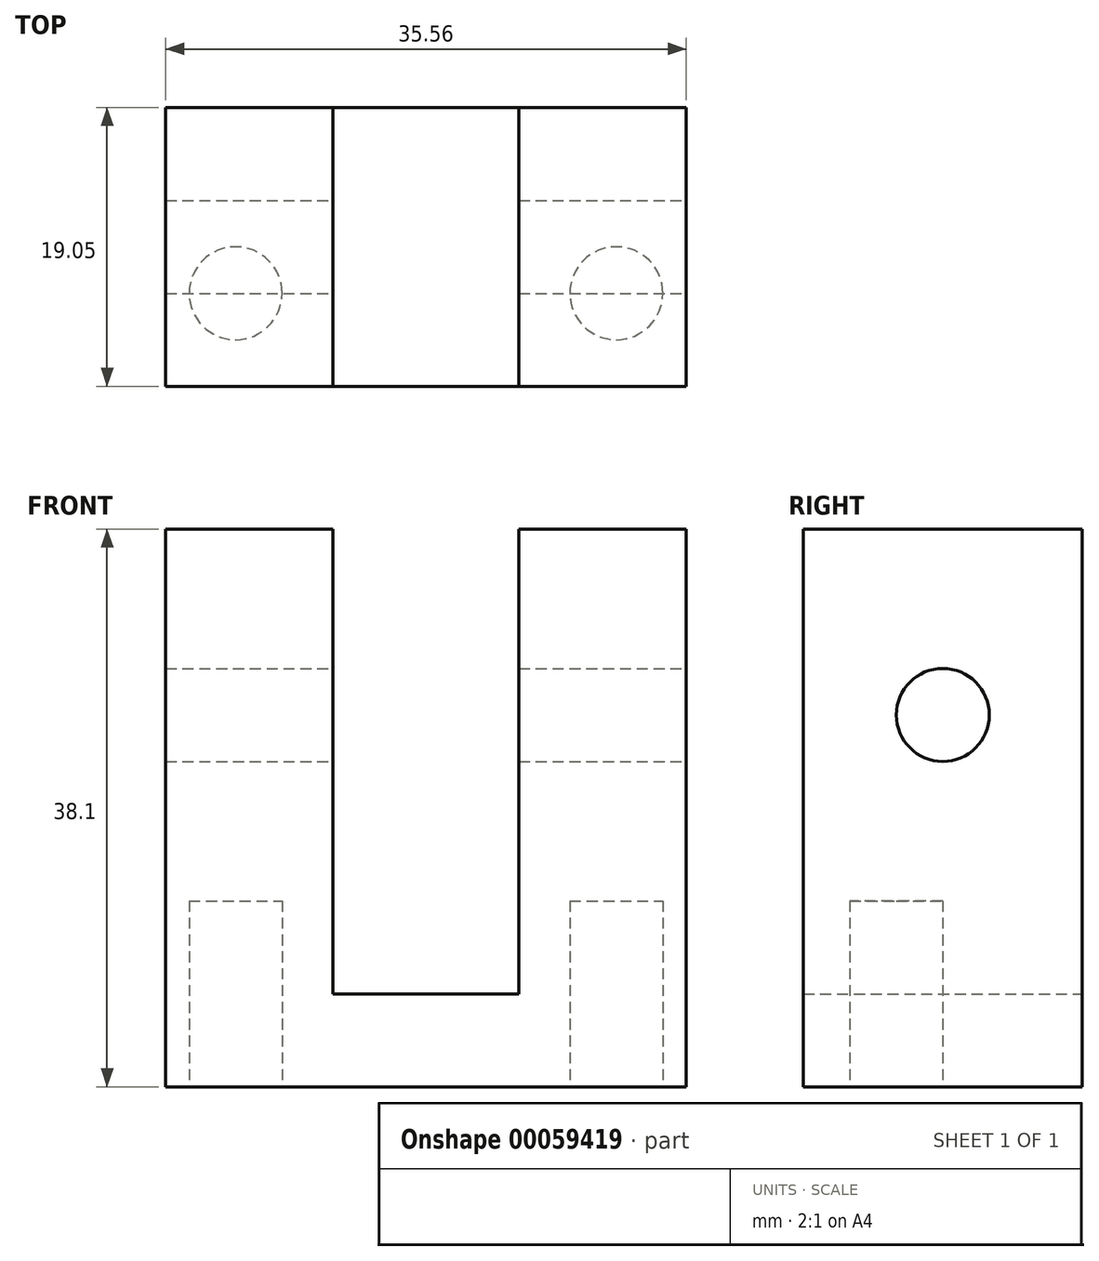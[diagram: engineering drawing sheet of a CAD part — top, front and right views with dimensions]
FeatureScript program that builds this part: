
annotation { "Feature Type Name" : "Feature", "Feature Type Description" : "" }
export const myFeature = defineFeature(function(context is Context, id is Id, definition is map)
    precondition{}
    {
        {
            var Q0;
            Q0=qCreatedBy(makeId("Front.planeOp"),FACE);
            var sketch = newSketch(context, id + "F0", { "sketchPlane" : qUnion([Q0])});
            skLineSegment(sketch, "E0.bottom", {"start": v(0, 0) * mm, "end": v(35.56, 0) * mm});
            skLineSegment(sketch, "E0.top", {"start": v(0, 38.1) * mm, "end": v(11.43, 38.1) * mm});
            skLineSegment(sketch, "E0.left", {"start": v(0, 0) * mm, "end": v(0, 38.1) * mm});
            skLineSegment(sketch, "E0.right", {"start": v(35.56, 0) * mm, "end": v(35.56, 38.1) * mm});
            skLineSegment(sketch, "E1", {"start": v(11.43, 38.1) * mm, "end": v(11.43, 6.35) * mm});
            skLineSegment(sketch, "E2", {"start": v(11.43, 6.35) * mm, "end": v(24.13, 6.35) * mm});
            skLineSegment(sketch, "E3", {"start": v(24.13, 6.35) * mm, "end": v(24.13, 38.1) * mm});
            skLineSegment(sketch, "E4.trimOffspring", {"start": v(24.13, 38.1) * mm, "end": v(35.56, 38.1) * mm});
            skSolve(sketch);
        }
        {
            var Q0;
            Q0 = qSketchRegion(id + "F0", true);
            extrude(context, id + "F1", {"entities" : qUnion([Q0]), "depth" : 19.05 * mm});
        }
        {
            var Q0;
            Q0=makeQuery(id+"F1.opExtrude","SWEPT_FACE",FACE,{"disambiguationData":[OSD([sQuery(id+"F0.wireOp",EDGE,"E0.right")])]});
            var sketch = newSketch(context, id + "F2", { "sketchPlane" : qUnion([Q0])});
            skCircle(sketch, "E5", {"center": v(-9.53, 25.4) * mm, "radius": 3.18 * mm});
            skSolve(sketch);
        }
        {
            var Q0;
            Q0 = qSketchRegion(id + "F2", true);
            var Q1;
            Q1=makeQuery(id+"F2.imprint","IMPRINT",FACE,{"disambiguationData":[TD([[makeQuery(id+"F2.imprint","IMPRINT",EDGE,{"derivedFrom":sQuery(id+"F2.wireOp",EDGE,"E5")}),1.0]])]});
            extrude(context, id + "F3", {"entities" : qUnion([Q0, Q1]), "operationType" : NewBodyOperationType.REMOVE, "endBound" : BoundingType.THROUGH_ALL, "oppositeDirection" : true, "depth" : 25.4 * mm});
        }
        {
            var Q0;
            Q0=makeQuery(id+"F1.opExtrude","SWEPT_FACE",FACE,{"disambiguationData":[OSD([sQuery(id+"F0.wireOp",EDGE,"E0.bottom")])]});
            var sketch = newSketch(context, id + "F4", { "sketchPlane" : qUnion([Q0])});
            skCircle(sketch, "E6", {"center": v(4.78, 12.7) * mm, "radius": 3.18 * mm});
            skCircle(sketch, "E7", {"center": v(30.78, 12.7) * mm, "radius": 3.18 * mm});
            skSolve(sketch);
        }
        {
            var Q0;
            Q0 = qSketchRegion(id + "F4", true);
            extrude(context, id + "F5", {"entities" : qUnion([Q0]), "operationType" : NewBodyOperationType.REMOVE, "oppositeDirection" : true, "depth" : 12.7 * mm});
        }
    });
